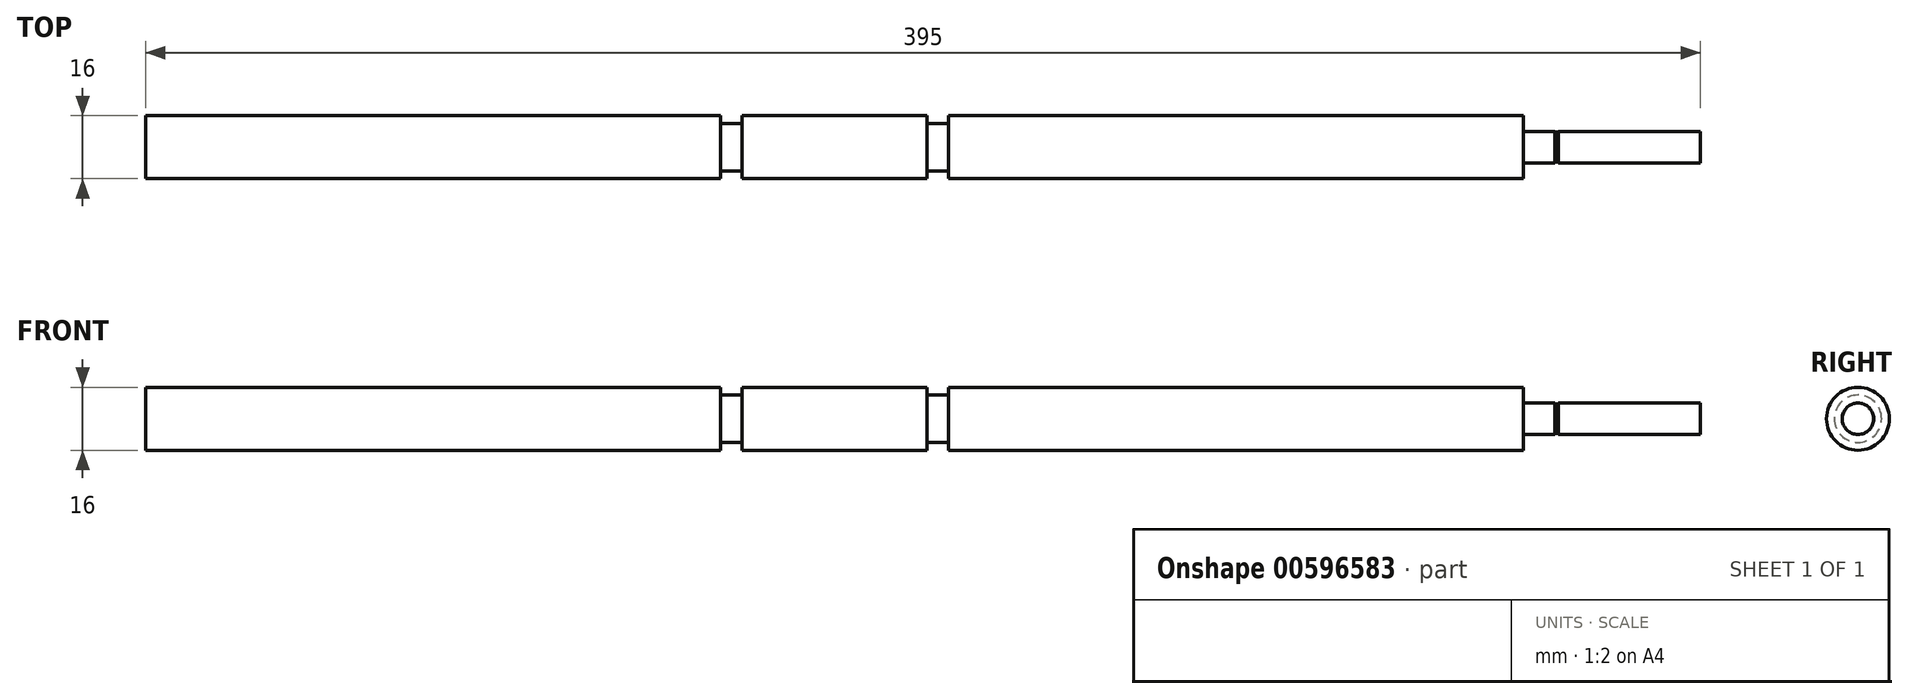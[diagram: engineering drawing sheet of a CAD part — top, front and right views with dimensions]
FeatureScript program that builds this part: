
annotation { "Feature Type Name" : "Feature", "Feature Type Description" : "" }
export const myFeature = defineFeature(function(context is Context, id is Id, definition is map)
    precondition{}
    {
        {
            var Q0;
            Q0=qCreatedBy(makeId("Front.planeOp"),FACE);
            var sketch = newSketch(context, id + "F0", { "sketchPlane" : qUnion([Q0])});
            skLineSegment(sketch, "E0.top", {"start": v(0, 16) * mm, "end": v(146, 16) * mm});
            skLineSegment(sketch, "E1.0", {"start": v(204, 16) * mm, "end": v(204, 14) * mm});
            skLineSegment(sketch, "E2.0", {"start": v(350, 16) * mm, "end": v(350, 12) * mm});
            skLineSegment(sketch, "E3.0", {"start": v(198.5, 16) * mm, "end": v(198.5, 14) * mm});
            skLineSegment(sketch, "E4.trimOffspring", {"start": v(151.5, 16) * mm, "end": v(198.5, 16) * mm});
            skLineSegment(sketch, "E5.trimOffspring", {"start": v(204, 16) * mm, "end": v(350, 16) * mm});
            skLineSegment(sketch, "E6.0", {"start": v(146, 14) * mm, "end": v(151.5, 14) * mm});
            skLineSegment(sketch, "E7", {"start": v(198.5, 14) * mm, "end": v(204, 14) * mm});
            skLineSegment(sketch, "E8", {"start": v(358, 8) * mm, "end": v(358.9, 8) * mm});
            skLineSegment(sketch, "E9.0", {"start": v(350, 12) * mm, "end": v(358, 12) * mm});
            skLineSegment(sketch, "E10.0", {"start": v(358, 12) * mm, "end": v(358, 11.8) * mm});
            skLineSegment(sketch, "E11.0", {"start": v(358.9, 12) * mm, "end": v(358.9, 11.8) * mm});
            skLineSegment(sketch, "E12.0", {"start": v(358, 11.8) * mm, "end": v(358.9, 11.8) * mm});
            skLineSegment(sketch, "E13.trimOffspring", {"start": v(358.9, 12) * mm, "end": v(395, 12) * mm});
            skLineSegment(sketch, "E14", {"start": v(146, 16) * mm, "end": v(146, 14) * mm});
            skLineSegment(sketch, "E15", {"start": v(151.5, 16) * mm, "end": v(151.5, 14) * mm});
            skLineSegment(sketch, "E16", {"start": v(395, 12) * mm, "end": v(395, 8) * mm});
            skLineSegment(sketch, "E17", {"start": v(0, 16) * mm, "end": v(0, 8) * mm});
            skLineSegment(sketch, "E18", {"start": v(0, 8) * mm, "end": v(395, 8) * mm});
            skSolve(sketch);
        }
        {
            var Q0;
            Q0 = qSketchRegion(id + "F0", true);
            var Q1;
            Q1=sQuery(id+"F0.wireOp",EDGE,"E18");
            revolve(context, id + "F1", {"entities" : qUnion([Q0]), "axis" : qUnion([Q1]), "revolveType" : RevolveType.FULL});
        }
    });
